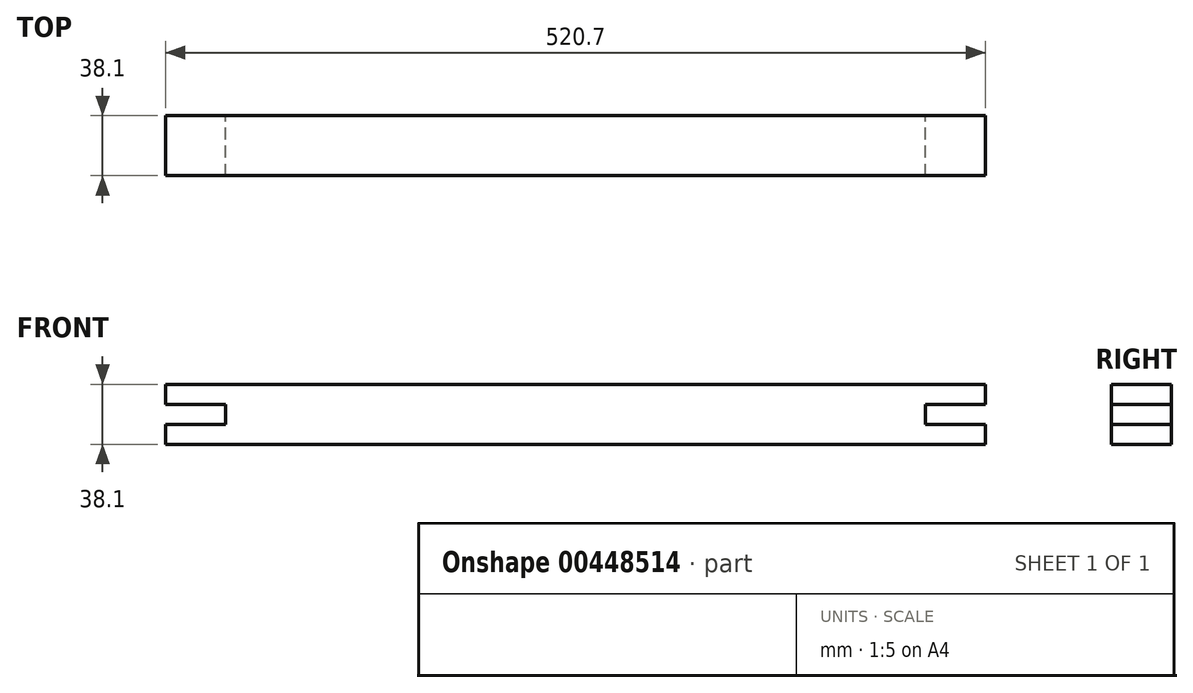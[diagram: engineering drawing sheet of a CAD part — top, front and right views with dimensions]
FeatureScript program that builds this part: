
annotation { "Feature Type Name" : "Feature", "Feature Type Description" : "" }
export const myFeature = defineFeature(function(context is Context, id is Id, definition is map)
    precondition{}
    {
        {
            var Q0;
            Q0=qCreatedBy(makeId("Front.planeOp"),FACE);
            var sketch = newSketch(context, id + "F0", { "sketchPlane" : qUnion([Q0])});
            skLineSegment(sketch, "E0.bottom", {"start": v(0, 0) * mm, "end": v(520.7, 0) * mm});
            skLineSegment(sketch, "E0.top", {"start": v(0, -38.1) * mm, "end": v(520.7, -38.1) * mm});
            skLineSegment(sketch, "E0.left", {"start": v(0, 0) * mm, "end": v(0, -12.7) * mm});
            skLineSegment(sketch, "E0.right", {"start": v(520.7, 0) * mm, "end": v(520.7, -12.7) * mm});
            skLineSegment(sketch, "E1", {"start": v(0, -12.7) * mm, "end": v(38.1, -12.7) * mm});
            skLineSegment(sketch, "E2", {"start": v(38.1, -12.7) * mm, "end": v(38.1, -25.4) * mm});
            skLineSegment(sketch, "E3", {"start": v(38.1, -25.4) * mm, "end": v(0, -25.4) * mm});
            skLineSegment(sketch, "E4.trimOffspring", {"start": v(0, -25.4) * mm, "end": v(0, -38.1) * mm});
            skLineSegment(sketch, "E5.bottom", {"start": v(520.7, -12.7) * mm, "end": v(482.6, -12.7) * mm});
            skLineSegment(sketch, "E5.top", {"start": v(520.7, -25.4) * mm, "end": v(482.6, -25.4) * mm});
            skLineSegment(sketch, "E5.right", {"start": v(482.6, -12.7) * mm, "end": v(482.6, -25.4) * mm});
            skLineSegment(sketch, "E6.trimOffspring", {"start": v(520.7, -25.4) * mm, "end": v(520.7, -38.1) * mm});
            skSolve(sketch);
        }
        {
            var Q0;
            Q0=makeQuery(id+"F0.imprint","IMPRINT",FACE,{"disambiguationData":[TD([[makeQuery(id+"F0.imprint","IMPRINT",EDGE,{"derivedFrom":sQuery(id+"F0.wireOp",EDGE,"E0.bottom")}),-1.0]])]});
            extrude(context, id + "F1", {"entities" : qUnion([Q0]), "depth" : 38.1 * mm});
        }
    });
